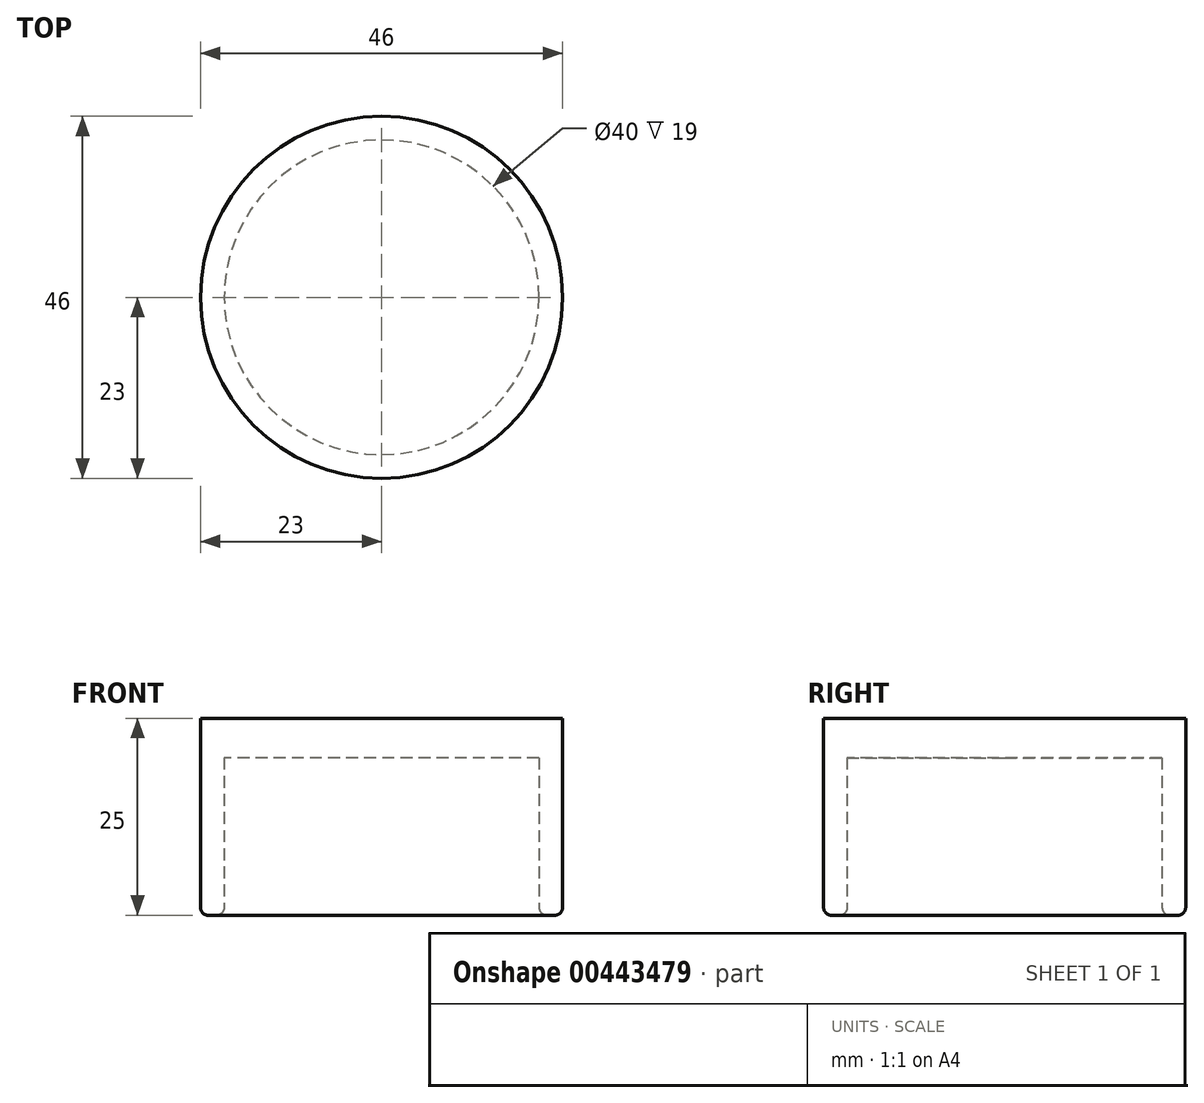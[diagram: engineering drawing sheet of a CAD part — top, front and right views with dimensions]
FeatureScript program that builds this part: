
annotation { "Feature Type Name" : "Feature", "Feature Type Description" : "" }
export const myFeature = defineFeature(function(context is Context, id is Id, definition is map)
    precondition{}
    {
        {
            var Q0;
            Q0=qCreatedBy(makeId("Top.planeOp"),FACE);
            var sketch = newSketch(context, id + "F0", { "sketchPlane" : qUnion([Q0])});
            skCircle(sketch, "E0", {"center": v(0, 0) * mm, "radius": 20 * mm});
            skCircle(sketch, "E1", {"center": v(0, 0) * mm, "radius": 23 * mm});
            skSolve(sketch);
        }
        {
            var Q0;
            Q0=makeQuery(id+"F0.imprint","IMPRINT",FACE,{"disambiguationData":[TD([[makeQuery(id+"F0.imprint","IMPRINT",EDGE,{"derivedFrom":sQuery(id+"F0.wireOp",EDGE,"E0")}),-1.0]])]});
            extrude(context, id + "F1", {"entities" : qUnion([Q0]), "depth" : 20 * mm});
        }
        {
            var Q0;
            Q0=makeQuery(id+"F1.opExtrude","CAP_FACE",FACE,{"disambiguationData":[OSD([sQuery(id+"F0.wireOp",EDGE,"E0"),sQuery(id+"F0.wireOp",EDGE,"E1")])],"isStart":false});
            var sketch = newSketch(context, id + "F2", { "sketchPlane" : qUnion([Q0])});
            skCircle(sketch, "E2", {"center": v(0, 0) * mm, "radius": 23 * mm});
            skSolve(sketch);
        }
        {
            var Q0;
            Q0 = qSketchRegion(id + "F2", true);
            extrude(context, id + "F3", {"entities" : qUnion([Q0]), "operationType" : NewBodyOperationType.ADD, "depth" : 5 * mm});
        }
        {
            var Q0;
            Q0=makeQuery(id+"F1.opExtrude","CAP_EDGE",EDGE,{"disambiguationData":[OSD([sQuery(id+"F0.wireOp",EDGE,"E0")])],"isStart":true});
            fillet(context, id + "F4", {"entities" : qUnion([Q0]), "radius" : 1 * mm, "tangentPropagation" : true, "allowEdgeOverflow" : false});
        }
        {
            var Q0;
            Q0=makeQuery(id+"F1.opExtrude","CAP_EDGE",EDGE,{"disambiguationData":[OSD([sQuery(id+"F0.wireOp",EDGE,"E1")])],"isStart":true});
            fillet(context, id + "F5", {"entities" : qUnion([Q0]), "radius" : 1 * mm, "tangentPropagation" : true, "allowEdgeOverflow" : false});
        }
    });
